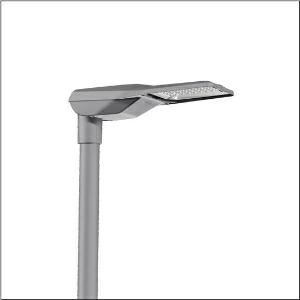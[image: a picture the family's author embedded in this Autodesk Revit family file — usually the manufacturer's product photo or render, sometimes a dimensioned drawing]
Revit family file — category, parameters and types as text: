
# Revit family: streetlight_sl_21_iq_mini___st1_0a_5xe2d41g08gb_82d1
name_source: partatom
category: Lighting Fixtures
units: mm (PartAtom-declared; Revit-internal decimal feet)

## family parameters
Cut with Voids When Loaded = No
Host = Face
Light Source = No
Part Type = Normal
Room Calculation Point = No
Round Connector Dimension = Use Diameter
Shared = No

## types (1)
- --- (1 x LED, 5920 lm, 37.1 W, 4000K)
    Apparent Load = 37 VA
    CIE Flux Codes = 37 72 97 100 100
    Color Rendering = 70
    Color Temperature = 4000K
    Default Elevation = 1800 mm
    Description = Streetlight SL 21 iQ mini, mast luminaire, primary light control with lens, of PMMA, primary optical cover: cover, of toughened safety glass, transparent, light distribution: ST1.0a, light emission: direct distribution, primary light characteristic: asymmetric, installation type: post-top, side-entry, LED, High Power LED, rated luminous flux: 5.920lm, luminous efficacy: 160lm/W, light colour: 740, colour temperature: 4000K, control: Street-Remote, Auto-Match, Temp-Guard, Lumen-Switch, Night-Set, Smart-Wire, Light-Fading, Desk-Remote (wireless, voltage-free reading and setting of iQ features in the workshop via application-optimized NFC function/RFID function), optimised constant luminous flux control (CLO 2.0), presetting dimming linear, mains connection: 220..240V, AC, 50/60Hz, start of lifetime: 37W, end of service life: 39W, reduction: 18W, luminaire housing, of diecast aluminium, powder-coated, Siteco® metallic grey (DB 702S), corrosivity category C5 mid according to DIN EN ISO 12944, please order mast flange separately, inclination adjustable: 0°, 5°, 10°, 15°, sealing non-destructively replaceable, multi-level sealing system, length: 628mm, width: 235mm, height: 110mm, mast flange for spigot size: 42mm (side-entry): 5XC10008XM4, 60/48mm (side-entry/post-top): 5XC10108XM2, 76/60mm (side-entry/post-top): 5XC10108XM1, protection rating (complete): IP66, insulation class (complete): insulation class II (safety insulation), certification: CE, ENEC, ENEC+, VDE, impact resistance: IK09, permissible operating ambient temperature for outdoor applications: -40..+50°C, standard-compliant lighting for roads and squares, packaging unit: 1 piece

Light Distribution: ST1.0a
    Height = 110 mm
    Lamp = 1 x LED
    Lamp Light Flux = 5920 lm
    Lamp Power = 37.1 W
    Lamp count = 1
    Length = 625 mm
    Luminous efficacy = 160 lm/W
    Manufacturer = Siteco
    ModVariant = No
    Model = 5XE2D41G08GB
    Number of Poles = 1
    OnlyDefault = Yes
    Power Factor = 1
    Product Name = Streetlight SL 21 iQ mini | ST1.0a
    Product group = mast luminaire | pylon top
    ProductGroupID = 6100
    Protection Class = Protection class II
    Protection Degree = IP 66
    RLX_Detail_Level = 1
    RLX_Emergency_Light_Flux = 0 lm
    RLX_Emergency_Type = 0
    RLX_Emergency_Type_DB = No
    RlxData = <blob elided: 92177 chars, md5=696bbbae>
    Socket = socket
    Standby Power = 0 W
    System Light Flux = 5920 lm
    System Power = 37 W
    Type Comments = factory setting: luminous flux: 100 % | dim-lin: 254 | 385 mA
    Type Image = l_1003519.jpg
    URL = http://relux.com
    VarID = @adj_122567
    Voltage = 0 V
    Weight = 0.00 kg
    Width = 234 mm

## geometry (parser evidence)
native form markers: Blend x4, Sweep x12
no freeform markers — native parametric forms only
